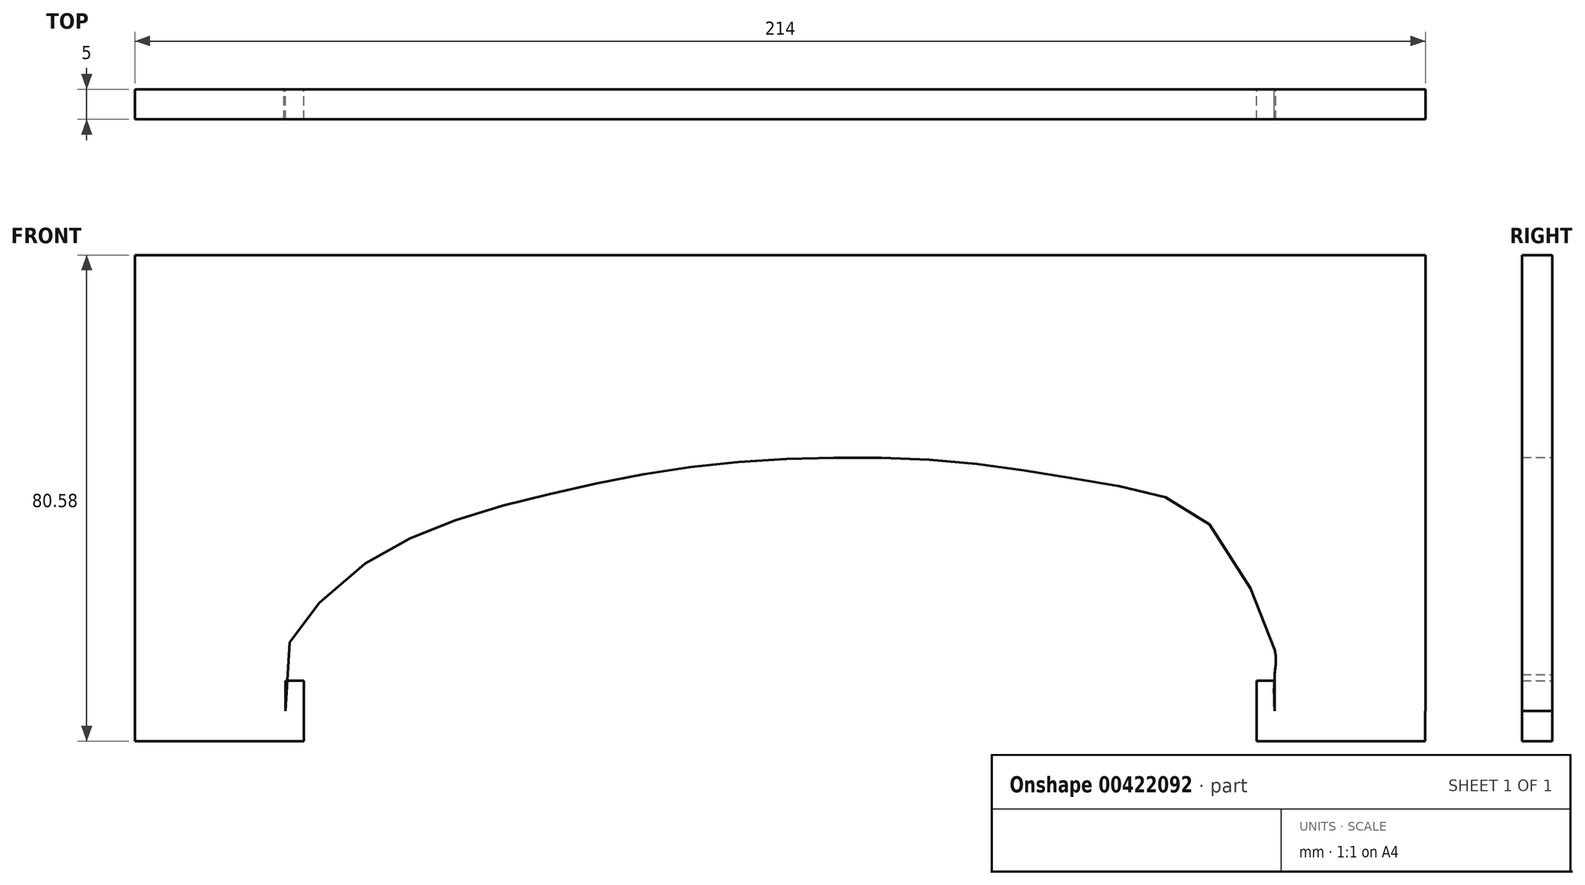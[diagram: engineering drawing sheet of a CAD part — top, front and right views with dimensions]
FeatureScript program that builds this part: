
annotation { "Feature Type Name" : "Feature", "Feature Type Description" : "" }
export const myFeature = defineFeature(function(context is Context, id is Id, definition is map)
    precondition{}
    {
        {
            var Q0;
            Q0=qCreatedBy(makeId("Front.planeOp"),FACE);
            var sketch = newSketch(context, id + "F0", { "sketchPlane" : qUnion([Q0])});
            skLineSegment(sketch, "E0", {"start": v(-155.15, 0) * mm, "end": v(159.47, 0) * mm});
            skFitSpline(sketch, "E1", {"points": [v(-136.78, 0) * mm, v(-133.83, 15) * mm, v(-122.78, 25) * mm, v(-112.78, 30) * mm, v(-102.78, 33.5) * mm, v(-92.78, 36) * mm, v(-82.78, 38.25) * mm, v(-72.78, 40) * mm, v(-62.78, 41.2) * mm, v(-52.78, 41.8) * mm, v(-42.78, 42) * mm, v(-32.78, 41.8) * mm, v(-22.78, 41) * mm, v(-12.78, 39.6) * mm, v(-2.78, 38) * mm, v(7.22, 36) * mm, v(17.22, 30) * mm, v(27.22, 10.16) * mm, v(27.22, 0) * mm], "startDerivative": vector(-35.65, 427.81) * mm, "endDerivative": vector(24.57, -417.64) * mm});
            skLineSegment(sketch, "E2", {"start": v(27.22, 0) * mm, "end": v(27.22, 58.63) * mm});
            skLineSegment(sketch, "E3.bottom", {"start": v(52.22, 0) * mm, "end": v(-161.78, 0) * mm});
            skLineSegment(sketch, "E3.top", {"start": v(52.22, 75.58) * mm, "end": v(-161.78, 75.58) * mm});
            skLineSegment(sketch, "E3.left", {"start": v(52.22, 0) * mm, "end": v(52.22, 75.58) * mm});
            skLineSegment(sketch, "E3.right", {"start": v(-161.78, 0) * mm, "end": v(-161.78, 75.58) * mm});
            skLineSegment(sketch, "E4.bottom", {"start": v(27.22, 0) * mm, "end": v(24.22, 0) * mm});
            skLineSegment(sketch, "E4.top", {"start": v(27.22, 5) * mm, "end": v(24.22, 5) * mm});
            skLineSegment(sketch, "E4.left", {"start": v(27.22, 0) * mm, "end": v(27.22, 5) * mm});
            skLineSegment(sketch, "E4.right", {"start": v(24.22, 0) * mm, "end": v(24.22, 5) * mm});
            skLineSegment(sketch, "E5.bottom", {"start": v(-136.78, 0) * mm, "end": v(-133.78, 0) * mm});
            skLineSegment(sketch, "E5.top", {"start": v(-136.78, 5) * mm, "end": v(-133.78, 5) * mm});
            skLineSegment(sketch, "E5.left", {"start": v(-136.78, 0) * mm, "end": v(-136.78, 5) * mm});
            skLineSegment(sketch, "E5.right", {"start": v(-133.78, 0) * mm, "end": v(-133.78, 5) * mm});
            skLineSegment(sketch, "E6.bottom", {"start": v(-133.78, 0) * mm, "end": v(24.14, 0) * mm});
            skLineSegment(sketch, "E6.top", {"start": v(-133.78, -5) * mm, "end": v(24.14, -5) * mm});
            skLineSegment(sketch, "E6.left", {"start": v(-133.78, 0) * mm, "end": v(-133.78, -5) * mm});
            skLineSegment(sketch, "E6.right", {"start": v(24.14, 0) * mm, "end": v(24.14, -5) * mm});
            skLineSegment(sketch, "E7.bottom", {"start": v(-151.86, 0) * mm, "end": v(-153.93, 0) * mm});
            skLineSegment(sketch, "E8.bottom", {"start": v(-161.78, 0) * mm, "end": v(-133.78, 0) * mm});
            skLineSegment(sketch, "E8.top", {"start": v(-161.78, -5) * mm, "end": v(-133.78, -5) * mm});
            skLineSegment(sketch, "E8.left", {"start": v(-161.78, 0) * mm, "end": v(-161.78, -5) * mm});
            skLineSegment(sketch, "E9.bottom", {"start": v(24.22, 0) * mm, "end": v(52.14, 0) * mm});
            skLineSegment(sketch, "E9.top", {"start": v(24.22, -5) * mm, "end": v(52.14, -5) * mm});
            skLineSegment(sketch, "E9.left", {"start": v(24.22, 0) * mm, "end": v(24.22, -5) * mm});
            skLineSegment(sketch, "E9.right", {"start": v(52.14, 0) * mm, "end": v(52.14, -5) * mm});
            skSolve(sketch);
        }
        {
            var Q0;
            Q0=makeQuery(id+"F0.imprint","IMPRINT",FACE,{"disambiguationData":[TD([[makeQuery(id+"F0.imprint","IMPRINT",EDGE,{"derivedFrom":sQuery(id+"F0.wireOp",EDGE,"E8.top")}),1.0]])]});
            var Q1;
            Q1=makeQuery(id+"F0.imprint","IMPRINT",FACE,{"disambiguationData":[TD([[makeQuery(id+"F0.imprint","IMPRINT",EDGE,{"derivedFrom":sQuery(id+"F0.wireOp",EDGE,"E5.top")}),-1.0]])]});
            var Q2;
            Q2=makeQuery(id+"F0.imprint","IMPRINT",FACE,{"disambiguationData":[TD([[makeQuery(id+"F0.imprint","IMPRINT",EDGE,{"derivedFrom":sQuery(id+"F0.wireOp",EDGE,"E3.top")}),1.0]])]});
            var Q3;
            {var subQ5=sQuery(id+"F0.wireOp",EDGE,"E4.right");Q3=makeQuery(id+"F0.imprint","IMPRINT",FACE,{"disambiguationData":[TD([[makeQuery(id+"F0.imprint","IMPRINT",EDGE,{"derivedFrom":subQ5}),-1.0]])]});}
            var Q4;
            Q4=makeQuery(id+"F0.imprint","IMPRINT",FACE,{"disambiguationData":[TD([[makeQuery(id+"F0.imprint","IMPRINT",EDGE,{"derivedFrom":sQuery(id+"F0.wireOp",EDGE,"E9.top")}),1.0]])]});
            extrude(context, id + "F1", {"entities" : qUnion([Q0, Q1, Q2, Q3, Q4]), "depth" : 5 * mm, "offsetDistance" : 25 * mm});
        }
    });
